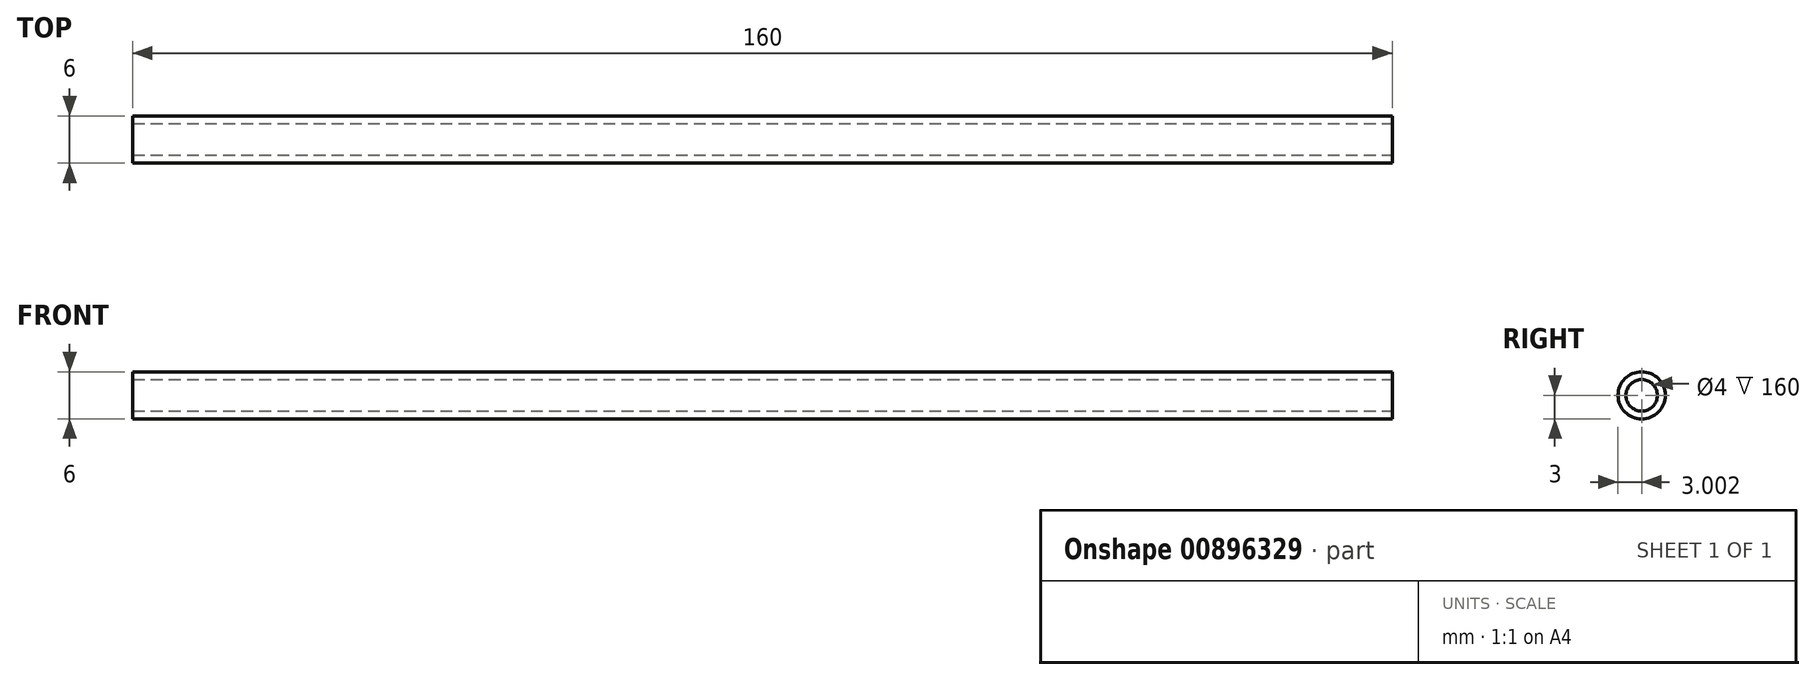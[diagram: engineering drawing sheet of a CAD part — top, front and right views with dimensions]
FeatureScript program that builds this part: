
annotation { "Feature Type Name" : "Feature", "Feature Type Description" : "" }
export const myFeature = defineFeature(function(context is Context, id is Id, definition is map)
    precondition{}
    {
        {
            var Q0;
            Q0=qCreatedBy(makeId("Top.planeOp"),FACE);
            var sketch = newSketch(context, id + "F0", { "sketchPlane" : qUnion([Q0])});
            skLineSegment(sketch, "E0.bottom", {"start": v(-79.06, 17.33) * mm, "end": v(80.94, 17.33) * mm});
            skLineSegment(sketch, "E0.top", {"start": v(-79.06, 11.33) * mm, "end": v(80.94, 11.33) * mm});
            skLineSegment(sketch, "E0.left", {"start": v(-79.06, 17.33) * mm, "end": v(-79.06, 11.33) * mm});
            skLineSegment(sketch, "E0.right", {"start": v(80.94, 17.33) * mm, "end": v(80.94, 11.33) * mm});
            skSolve(sketch);
        }
        {
            var Q0;
            Q0=makeQuery(id+"F0.imprint","IMPRINT",FACE,{"disambiguationData":[TD([[makeQuery(id+"F0.imprint","IMPRINT",EDGE,{"derivedFrom":sQuery(id+"F0.wireOp",EDGE,"E0.bottom")}),-1.0]])]});
            extrude(context, id + "F1", {"entities" : qUnion([Q0]), "depth" : 6 * mm, "offsetDistance" : 25 * mm});
        }
        {
            var Q0;
            Q0=makeQuery(id+"F1.opExtrude","CAP_EDGE",EDGE,{"disambiguationData":[OSD([sQuery(id+"F0.wireOp",EDGE,"E0.bottom")])],"isStart":false});
            var Q1;
            Q1=makeQuery(id+"F1.opExtrude","CAP_EDGE",EDGE,{"disambiguationData":[OSD([sQuery(id+"F0.wireOp",EDGE,"E0.top")])],"isStart":false});
            var Q2;
            Q2=makeQuery(id+"F1.opExtrude","CAP_EDGE",EDGE,{"disambiguationData":[OSD([sQuery(id+"F0.wireOp",EDGE,"E0.bottom")])],"isStart":true});
            var Q3;
            Q3=makeQuery(id+"F1.opExtrude","CAP_EDGE",EDGE,{"disambiguationData":[OSD([sQuery(id+"F0.wireOp",EDGE,"E0.top")])],"isStart":true});
            fillet(context, id + "F2", {"entities" : qUnion([Q0, Q1, Q2, Q3]), "radius" : 3 * mm, "tangentPropagation" : true, "allowEdgeOverflow" : false});
        }
        {
            var Q0;
            Q0=makeQuery(id+"F1.opExtrude","SWEPT_FACE",FACE,{"disambiguationData":[OSD([sQuery(id+"F0.wireOp",EDGE,"E0.right")])]});
            var sketch = newSketch(context, id + "F3", { "sketchPlane" : qUnion([Q0])});
            skPoint(sketch, "E1", {"position": v(14.33, 3) * mm});
            skSolve(sketch);
        }
        {
            var Q0;
            Q0=sQuery(id+"F3.wireOp",VERTEX,"E1");
            var Q1;
            Q1=makeQuery(id+"F1.opExtrude","SWEPT_BODY",BODY,{"disambiguationData":[OSD([sQuery(id+"F0.wireOp",EDGE,"E0.bottom"),sQuery(id+"F0.wireOp",EDGE,"E0.top"),sQuery(id+"F0.wireOp",EDGE,"E0.left"),sQuery(id+"F0.wireOp",EDGE,"E0.right")])]});
            hole(context, id + "F4", {"style" : HoleStyle.SIMPLE, "endStyle" : HoleEndStyle.THROUGH, "holeDiameter" : 4 * mm, "majorDiameter" : 5 * mm, "isTappedThrough" : true, "tappedDepth" : 12 * mm, "tapClearance" : 3, "locations" : qUnion([Q0]), "scope" : qUnion([Q1])});
        }
    });
